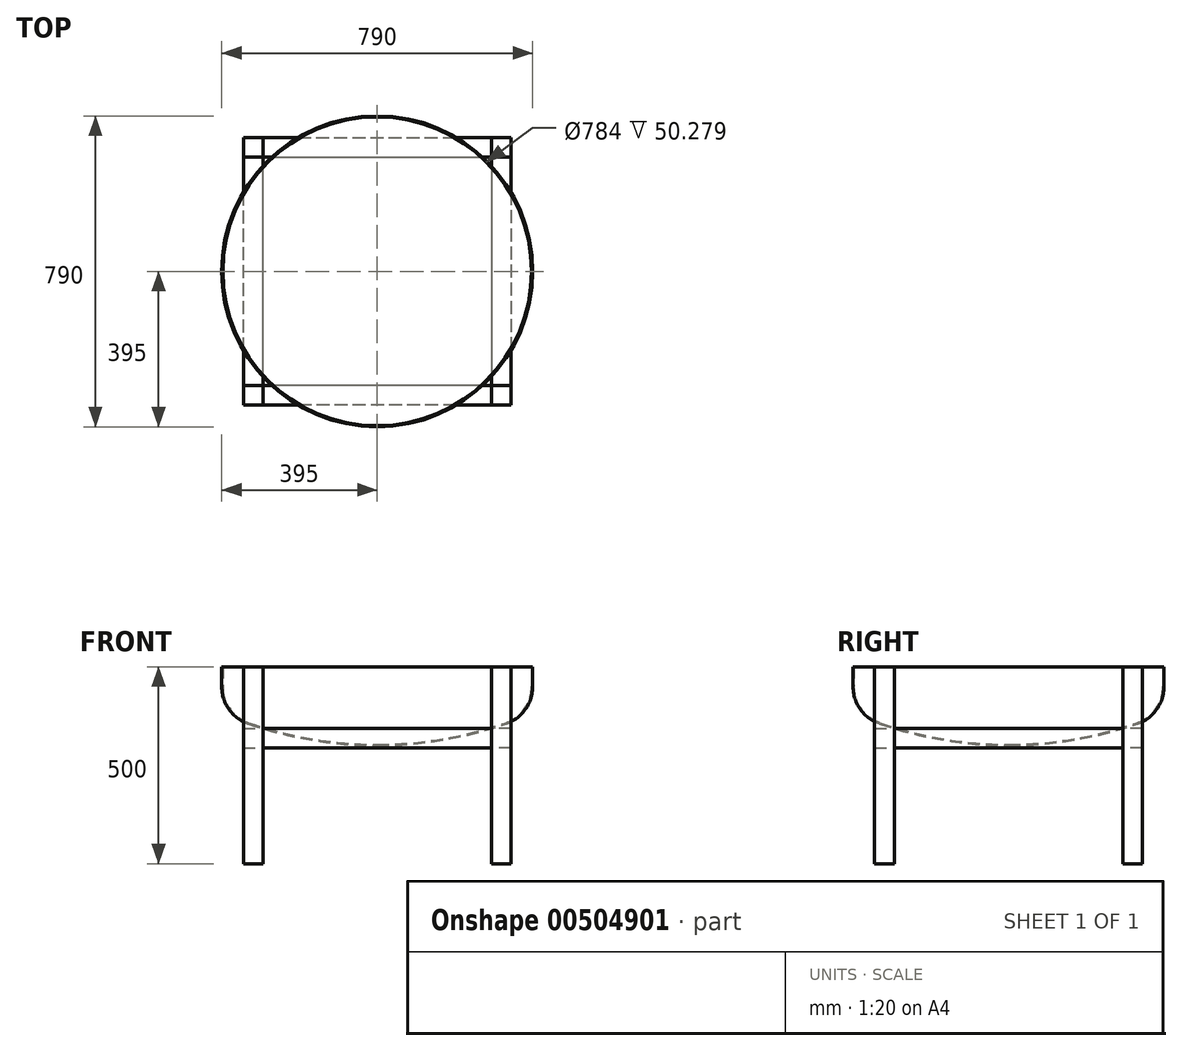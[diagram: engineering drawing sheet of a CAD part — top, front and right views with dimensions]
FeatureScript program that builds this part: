
annotation { "Feature Type Name" : "Feature", "Feature Type Description" : "" }
export const myFeature = defineFeature(function(context is Context, id is Id, definition is map)
    precondition{}
    {
        {
            var Q0;
            Q0=qCreatedBy(makeId("Top.planeOp"),FACE);
            var sketch = newSketch(context, id + "F0", { "sketchPlane" : qUnion([Q0])});
            skCircle(sketch, "E0", {"center": v(0, 0) * mm, "radius": 395 * mm});
            skLineSegment(sketch, "E1.bottom", {"start": v(-340, 340) * mm, "end": v(-290, 340) * mm});
            skLineSegment(sketch, "E1.top", {"start": v(-340, 290) * mm, "end": v(-290, 290) * mm});
            skLineSegment(sketch, "E1.left", {"start": v(-340, 340) * mm, "end": v(-340, 290) * mm});
            skLineSegment(sketch, "E1.right", {"start": v(-290, 340) * mm, "end": v(-290, 290) * mm});
            skSolve(sketch);
        }
        {
            var Q0;
            Q0=makeQuery(id+"F0.imprint","IMPRINT",FACE,{"disambiguationData":[TD([[makeQuery(id+"F0.imprint","IMPRINT",EDGE,{"derivedFrom":sQuery(id+"F0.wireOp",EDGE,"E1.bottom")}),-1.0]])]});
            extrude(context, id + "F1", {"entities" : qUnion([Q0]), "depth" : 500 * mm, "offsetDistance" : 25 * mm});
        }
        {
            var Q0;
            Q0=makeQuery(id+"F1.opExtrude","SWEPT_BODY",BODY,{"disambiguationData":[OSD([sQuery(id+"F0.wireOp",EDGE,"E1.bottom"),sQuery(id+"F0.wireOp",EDGE,"E1.top"),sQuery(id+"F0.wireOp",EDGE,"E1.left"),sQuery(id+"F0.wireOp",EDGE,"E1.right")])]});
            var Q1;
            Q1=sQuery(id+"F0.wireOp",EDGE,"E0");
            circularPattern(context, id + "F2", {"entities" : qUnion([Q0]), "axis" : qUnion([Q1]), "angle" : 360 * degree, "instanceCount" : 4, "equalSpace" : true, "isCentered" : true});
        }
        {
            var Q0;
            Q0=qCreatedBy(makeId("Top.planeOp"),FACE);
            cPlane(context, id + "F3", {"entities" : qUnion([Q0]), "cplaneType" : CPlaneType.OFFSET, "offset" : 294 * mm, "width" : 150 * mm, "height" : 150 * mm});
        }
        {
            var Q0;
            Q0=qCreatedBy(id+"F3.planeOp",FACE);
            var sketch = newSketch(context, id + "F4", { "sketchPlane" : qUnion([Q0])});
            skLineSegment(sketch, "E2.bottom", {"start": v(-290, 340) * mm, "end": v(290, 340) * mm});
            skLineSegment(sketch, "E2.top", {"start": v(-290, 290) * mm, "end": v(290, 290) * mm});
            skLineSegment(sketch, "E2.left", {"start": v(-290, 340) * mm, "end": v(-290, 290) * mm});
            skLineSegment(sketch, "E2.right", {"start": v(290, 340) * mm, "end": v(290, 290) * mm});
            skSolve(sketch);
        }
        {
            var Q0;
            Q0 = qSketchRegion(id + "F4", true);
            extrude(context, id + "F5", {"entities" : qUnion([Q0]), "depth" : 50 * mm, "offsetDistance" : 25 * mm});
        }
        {
            var Q0;
            Q0=makeQuery(id+"F5.opExtrude","SWEPT_BODY",BODY,{"disambiguationData":[OSD([sQuery(id+"F4.wireOp",EDGE,"E2.bottom"),sQuery(id+"F4.wireOp",EDGE,"E2.top"),sQuery(id+"F4.wireOp",EDGE,"E2.left"),sQuery(id+"F4.wireOp",EDGE,"E2.right")])]});
            var Q1;
            Q1=sQuery(id+"F0.wireOp",EDGE,"E0");
            circularPattern(context, id + "F6", {"entities" : qUnion([Q0]), "axis" : qUnion([Q1]), "angle" : 360 * degree, "instanceCount" : 4, "equalSpace" : true});
        }
        {
            var Q0;
            Q0=qCreatedBy(makeId("Front.planeOp"),FACE);
            var sketch = newSketch(context, id + "F7", { "sketchPlane" : qUnion([Q0])});
            skLineSegment(sketch, "E3", {"start": v(-395, 500) * mm, "end": v(-395, 449.72) * mm});
            skArc(sketch, "E4", {"start": v(-395, 449.72) * mm, "mid": v(-376.48, 391.75) * mm, "end": v(-327.78, 355.25) * mm});
            skArc(sketch, "E5", {"start": v(-327.78, 355.25) * mm, "mid": v(-166.2, 313.9) * mm, "end": v(0, 300) * mm});
            skLineSegment(sketch, "E6", {"start": v(0, 300) * mm, "end": v(137.5, 300) * mm, "construction": true});
            skLineSegment(sketch, "E7", {"start": v(-395, 500) * mm, "end": v(-392, 500) * mm});
            skLineSegment(sketch, "E8", {"start": v(0, 300) * mm, "end": v(0, 303) * mm});
            skArc(sketch, "E9.0", {"start": v(-326.8, 358.08) * mm, "mid": v(-165.7, 316.87) * mm, "end": v(0, 303) * mm});
            skArc(sketch, "E9.1", {"start": v(-392, 449.72) * mm, "mid": v(-374.03, 393.48) * mm, "end": v(-326.8, 358.08) * mm});
            skLineSegment(sketch, "E9.2", {"start": v(-392, 600) * mm, "end": v(-392, 449.72) * mm});
            skSolve(sketch);
        }
        {
            var Q0;
            Q0 = qSketchRegion(id + "F7", true);
            var Q1;
            Q1=sQuery(id+"F0.wireOp",EDGE,"E0");
            revolve(context, id + "F8", {"entities" : qUnion([Q0]), "axis" : qUnion([Q1]), "revolveType" : RevolveType.FULL});
        }
    });
